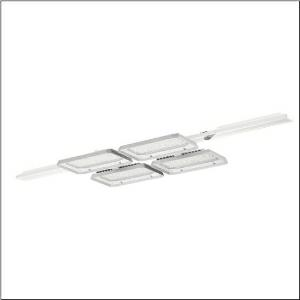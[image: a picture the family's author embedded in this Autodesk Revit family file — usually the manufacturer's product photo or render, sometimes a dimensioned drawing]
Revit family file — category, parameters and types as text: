
# Revit family: highbay_11_51hla1d24nla
name_source: partatom
category: Lighting Fixtures
units: mm (PartAtom-declared; Revit-internal decimal feet)

## family parameters
Cut with Voids When Loaded = No
Host = Face
Light Source = No
Part Type = Normal
Room Calculation Point = No
Round Connector Dimension = Use Diameter
Shared = No

## types (1)
- --- (1 x LED, 32370 lm, 189.7 W, 4000K)
    Apparent Load = 759 VA
    CIE Flux Codes = 88 95 99 100 99
    Color Rendering = 80
    Color Temperature = 4000K
    Default Elevation = 1800 mm
    Description = Highbay 11, LED high bay luminaire, end cap, primary light control with lens, of PMMA, light emission: direct distribution, primary light characteristic: symmetric, installation type: recessed, for 2x 2 x LED rated luminous flux: 32.370 lm, light colour: 840, colour temperature: 4000K, control gear: ECG DALI, with system connector, mains connection: 230..240V, AC, 50/60Hz, rated input power: 190W, LED unit, of diecast aluminium, unplated, bead blasted, silver, length: 1.500 mm, width: 500 mm, height: 65mm, housing, of diecast aluminium, uncoated, bead blasted, silver, fixing on rail side, of aluminium, anodised, metallic grey, end cap, of PC, grey, protection rating (complete): IP64, insulation class (complete): insulation class I (protective earthing), certification: CE, protection symbol: D, impact resistance: IK08 with glass or PC cover, permissible ambient temperature for indoor applications: -35..+45°C, corresponds to IFS (International Featured Standards) requirements for safety and quality in the food industry, packaging unit: 1 piece
    Height = 105 mm
    Lamp = 1 x LED
    Lamp Light Flux = 32370 lm
    Lamp Power = 189.7 W
    Lamp count = 1
    Length = 1500 mm
    Luminous efficacy = 171 lm/W
    Manufacturer = Siteco
    ModVariant = No
    Model = 51HLA1D24NLA
    Mounting Place = Ceiling
    Mounting Type = Pendant
    Number of Poles = 1
    OnlyDefault = Yes
    Power Factor = 1
    Product Name = Highbay 11
    Product group = LED high bay luminaire
    ProductGroupID = 903
    Protection Class = Protection class I
    Protection Degree = IP 64
    RLX_Detail_Level = 1
    RlxData = <blob elided: 87537 chars, md5=6ce86879>
    Socket = socket
    Standby Power = 0 W
    System Light Flux = 129480 lm
    System Power = 759 W
    Type Comments = factory setting: luminous flux: 100 % | dim-lin: 254 | 535 mA
    Type Image = l_1004707.jpg
    URL = http://relux.com
    VarID = @adj_137181
    Voltage = 0 V
    Weight = 0.00 kg
    Width = 500 mm

## geometry (parser evidence)
native form markers: Blend x4, Sweep x21
no freeform markers — native parametric forms only
